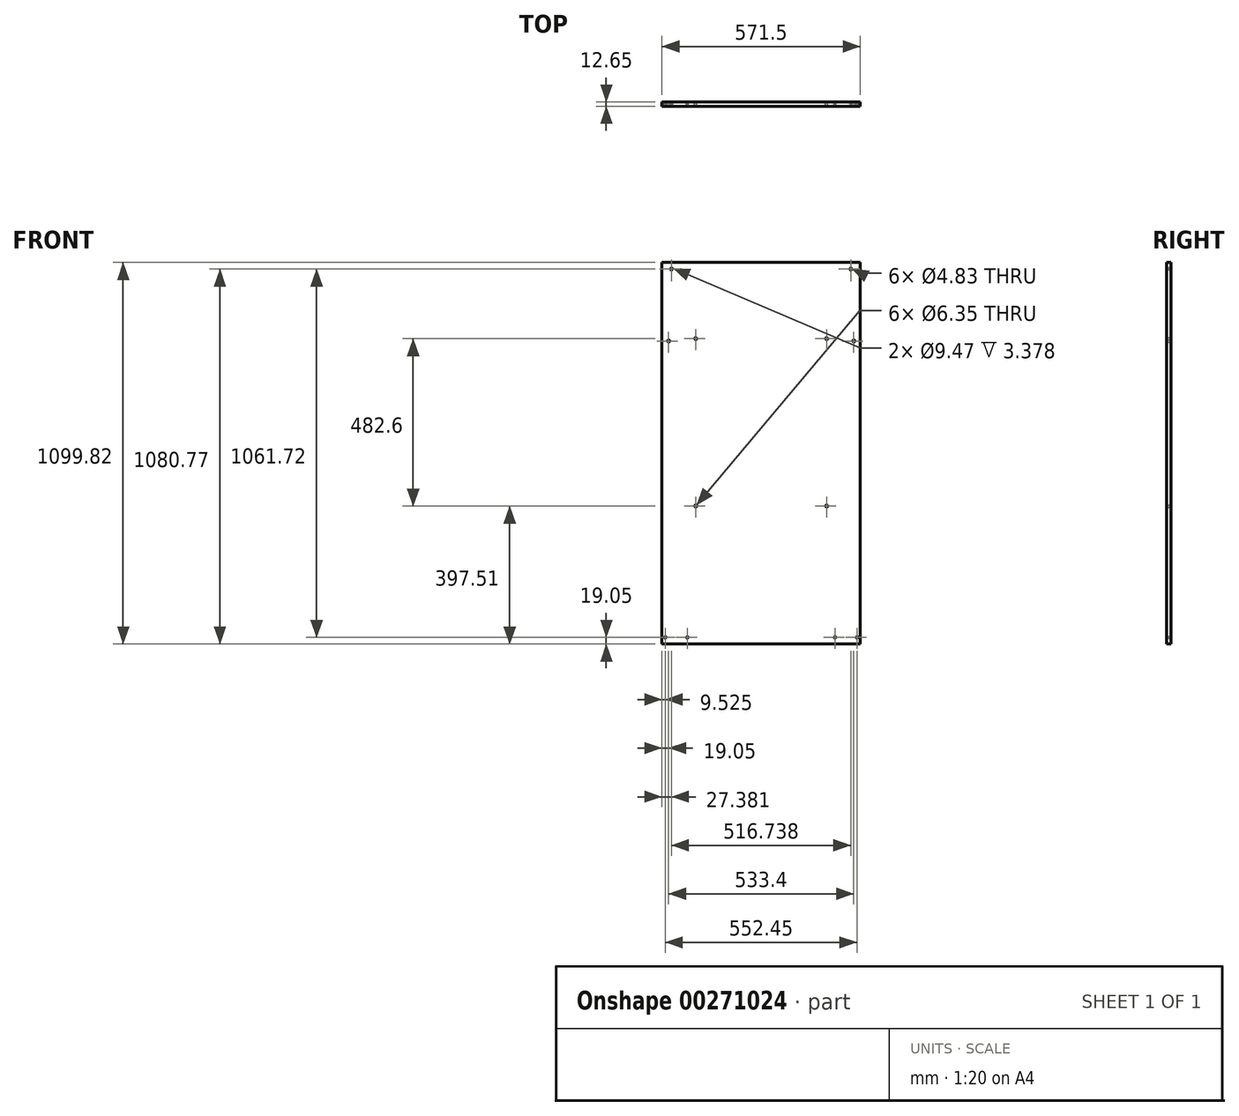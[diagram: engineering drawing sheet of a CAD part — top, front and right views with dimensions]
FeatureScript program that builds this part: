
annotation { "Feature Type Name" : "Feature", "Feature Type Description" : "" }
export const myFeature = defineFeature(function(context is Context, id is Id, definition is map)
    precondition{}
    {
        {
            var Q0;
            Q0=qCreatedBy(makeId("Front.planeOp"),FACE);
            var sketch = newSketch(context, id + "F0", { "sketchPlane" : qUnion([Q0])});
            skLineSegment(sketch, "E0.bottom", {"start": v(0, 0) * mm, "end": v(571.5, 0) * mm});
            skLineSegment(sketch, "E0.top", {"start": v(0, 1099.82) * mm, "end": v(571.5, 1099.82) * mm});
            skLineSegment(sketch, "E0.left", {"start": v(0, 0) * mm, "end": v(0, 1099.82) * mm});
            skLineSegment(sketch, "E0.right", {"start": v(571.5, 0) * mm, "end": v(571.5, 1099.82) * mm});
            skSolve(sketch);
        }
        {
            var Q0;
            Q0 = qSketchRegion(id + "F0", true);
            extrude(context, id + "F1", {"entities" : qUnion([Q0]), "depth" : 12.65 * mm});
        }
        {
            var Q0;
            Q0=makeQuery(id+"F1.opExtrude","CAP_FACE",FACE,{"disambiguationData":[OSD([sQuery(id+"F0.wireOp",EDGE,"E0.bottom"),sQuery(id+"F0.wireOp",EDGE,"E0.top"),sQuery(id+"F0.wireOp",EDGE,"E0.left"),sQuery(id+"F0.wireOp",EDGE,"E0.right")])],"isStart":false});
            var sketch = newSketch(context, id + "F2", { "sketchPlane" : qUnion([Q0])});
            skPoint(sketch, "E1", {"position": v(19.05, 873.13) * mm});
            skPoint(sketch, "E2", {"position": v(552.45, 873.13) * mm});
            skPoint(sketch, "E3", {"position": v(9.53, 19.05) * mm});
            skPoint(sketch, "E4", {"position": v(73.03, 19.05) * mm});
            skPoint(sketch, "E5", {"position": v(498.48, 19.05) * mm});
            skPoint(sketch, "E6", {"position": v(561.98, 19.05) * mm});
            skPoint(sketch, "E7", {"position": v(97.24, 880.1) * mm});
            skPoint(sketch, "E8", {"position": v(97.24, 397.5) * mm});
            skPoint(sketch, "E9", {"position": v(474.26, 880.1) * mm});
            skPoint(sketch, "E10", {"position": v(474.26, 397.5) * mm});
            skLineSegment(sketch, "E11", {"start": v(-128.07, 549.9) * mm, "end": v(783.92, 549.91) * mm, "construction": true});
            skPoint(sketch, "E11.startSnap0", {"position": v(0, 549.9) * mm});
            skSolve(sketch);
        }
        {
            var Q0;
            Q0=sQuery(id+"F2.wireOp",VERTEX,"E3");
            var Q1;
            Q1=sQuery(id+"F2.wireOp",VERTEX,"E4");
            var Q2;
            Q2=sQuery(id+"F2.wireOp",VERTEX,"E5");
            var Q3;
            Q3=sQuery(id+"F2.wireOp",VERTEX,"E6");
            var Q4;
            Q4=makeQuery(id+"F1.opExtrude","SWEPT_BODY",BODY,{"disambiguationData":[OSD([sQuery(id+"F0.wireOp",EDGE,"E0.bottom"),sQuery(id+"F0.wireOp",EDGE,"E0.top"),sQuery(id+"F0.wireOp",EDGE,"E0.left"),sQuery(id+"F0.wireOp",EDGE,"E0.right")])]});
            hole(context, id + "F3", {"style" : HoleStyle.SIMPLE, "endStyle" : HoleEndStyle.BLIND, "holeDiameter" : 4.83 * mm, "holeDepth" : 12.7 * mm, "tappedDepth" : 12.7 * mm, "tapClearance" : 3, "locations" : qUnion([Q0, Q1, Q2, Q3]), "scope" : qUnion([Q4])});
        }
        {
            var Q0;
            Q0=sQuery(id+"F2.wireOp",VERTEX,"E7");
            var Q1;
            Q1=sQuery(id+"F2.wireOp",VERTEX,"E9");
            var Q2;
            Q2=sQuery(id+"F2.wireOp",VERTEX,"E8");
            var Q3;
            Q3=sQuery(id+"F2.wireOp",VERTEX,"E10");
            var Q4;
            Q4=sQuery(id+"F2.wireOp",VERTEX,"E1");
            var Q5;
            Q5=sQuery(id+"F2.wireOp",VERTEX,"E2");
            var Q6;
            Q6=makeQuery(id+"F1.opExtrude","SWEPT_BODY",BODY,{"disambiguationData":[OSD([sQuery(id+"F0.wireOp",EDGE,"E0.bottom"),sQuery(id+"F0.wireOp",EDGE,"E0.top"),sQuery(id+"F0.wireOp",EDGE,"E0.left"),sQuery(id+"F0.wireOp",EDGE,"E0.right")])]});
            hole(context, id + "F4", {"style" : HoleStyle.SIMPLE, "endStyle" : HoleEndStyle.THROUGH, "holeDiameter" : 6.35 * mm, "tappedDepth" : 12.7 * mm, "tapClearance" : 3, "locations" : qUnion([Q0, Q1, Q2, Q3, Q4, Q5]), "scope" : qUnion([Q6])});
        }
        {
            var Q0;
            Q0=makeQuery(id+"F1.opExtrude","CAP_FACE",FACE,{"disambiguationData":[OSD([sQuery(id+"F0.wireOp",EDGE,"E0.bottom"),sQuery(id+"F0.wireOp",EDGE,"E0.top"),sQuery(id+"F0.wireOp",EDGE,"E0.left"),sQuery(id+"F0.wireOp",EDGE,"E0.right")])],"isStart":true});
            var sketch = newSketch(context, id + "F5", { "sketchPlane" : qUnion([Q0])});
            skPoint(sketch, "E12", {"position": v(-544.12, 1080.77) * mm});
            skPoint(sketch, "E13", {"position": v(-27.38, 1080.77) * mm});
            skSolve(sketch);
        }
        {
            var Q0;
            Q0=sQuery(id+"F5.wireOp",VERTEX,"E12");
            var Q1;
            Q1=sQuery(id+"F5.wireOp",VERTEX,"E13");
            var Q2;
            Q2=makeQuery(id+"F1.opExtrude","SWEPT_BODY",BODY,{"disambiguationData":[OSD([sQuery(id+"F0.wireOp",EDGE,"E0.bottom"),sQuery(id+"F0.wireOp",EDGE,"E0.top"),sQuery(id+"F0.wireOp",EDGE,"E0.left"),sQuery(id+"F0.wireOp",EDGE,"E0.right")])]});
            hole(context, id + "F6", {"style" : HoleStyle.C_BORE, "endStyle" : HoleEndStyle.BLIND, "holeDiameter" : 4.83 * mm, "cBoreDiameter" : 9.47 * mm, "cBoreDepth" : 3.38 * mm, "holeDepth" : 12.7 * mm, "tappedDepth" : 12.7 * mm, "tapClearance" : 3, "locations" : qUnion([Q0, Q1]), "scope" : qUnion([Q2])});
        }
    });
